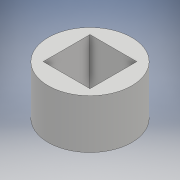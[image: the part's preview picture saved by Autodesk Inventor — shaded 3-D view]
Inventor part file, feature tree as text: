
AUTODESK INVENTOR PART (.ipt)
format: ipt  version: 2017 (Build 210142000, 142)  size: 95,232 bytes
history: native  units: mm
features: extrude x1, sketch x1
ambient origin geometry x8: Origin, YZ Plane, XZ Plane, XY Plane, X Axis, Y Axis, Z Axis, Center Point
bodies: Solid1 (feature_tree)
feature tree (2):
  extrude  "Extrusion1"  Depth=10.0mm
  sketch  "Sketch1"  dims[d0=9.525mm d1=17.0mm d2=10.0mm d3=0.0mm]
